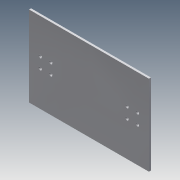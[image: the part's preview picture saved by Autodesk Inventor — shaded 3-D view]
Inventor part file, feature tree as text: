
AUTODESK INVENTOR PART (.ipt)
format: ipt  version: 2016 (Build 200138000, 138)  size: 108,544 bytes
history: native  units: in
note: dims shown in document units (in); Inventor stores cm internally (conversion verified against a paired STEP export)
features: extrude x1, hole x1, pattern_linear x1, plane x1, mirror x1, sketch x1
ambient origin geometry x8: Origin, YZ Plane, XZ Plane, XY Plane, X Axis, Y Axis, Z Axis, Center Point
bodies: Solid1 (feature_tree)
feature tree (6):
  extrude  "Extrusion1"  Depth=7.8346in
  hole  "Hole1"  [1 undecoded]
  pattern_linear  "Rectangular Pattern1"  Spacing1=0.8716in  [1 undecoded]
  plane  "Work Plane1"
  mirror  "Mirror1"
  sketch  "Sketch1"  dims[d0=11.6535in d1=7.8346in d2=0.7874in d4=1.0236in d5=0.7874in d7=1.0236in d10=0.8716in d12=0.1969in d13=0.0in d14=0.1969in d32=0.3937in d33=0.3937in d17=0.1772in d18=0.2362in d19=0.315in d20=0.0787in d21=90.0deg d22=0.315in d23=0.8108in d26=0.7874in d28=1.0236in d29=0.7874in d31=1.0236in]
note: 2 required parameter values undecoded (feature->parameter linkage not recoverable at this tier; creation-order binding heuristic only, values carry confidence <= 0.55)
